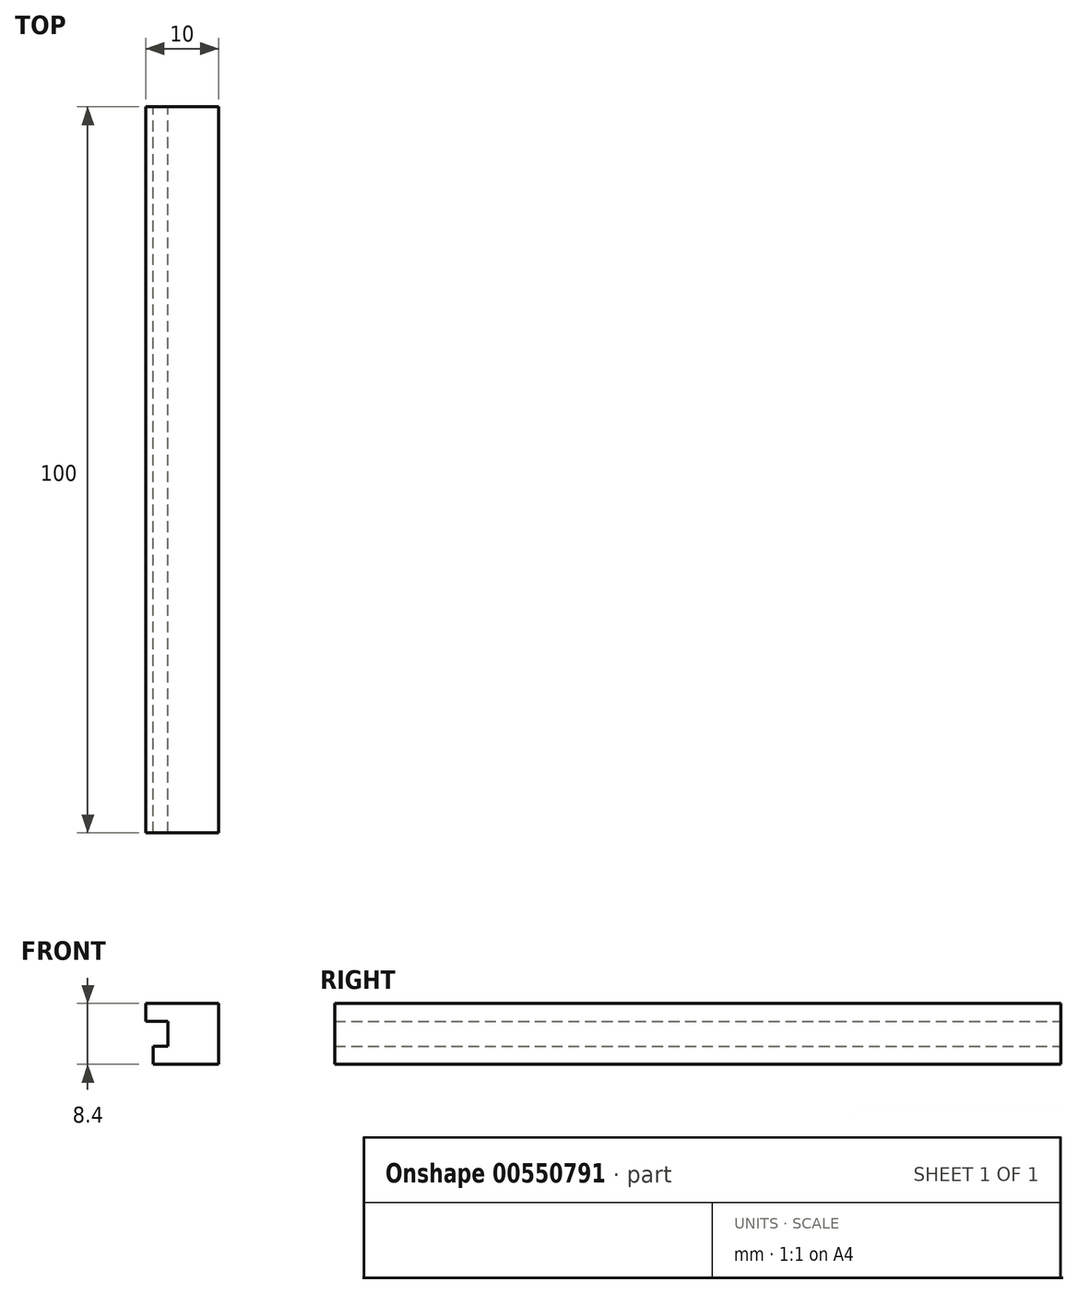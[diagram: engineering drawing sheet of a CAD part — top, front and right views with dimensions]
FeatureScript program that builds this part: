
annotation { "Feature Type Name" : "Feature", "Feature Type Description" : "" }
export const myFeature = defineFeature(function(context is Context, id is Id, definition is map)
    precondition{}
    {
        {
            var Q0;
            Q0=qCreatedBy(makeId("Front.planeOp"),FACE);
            var sketch = newSketch(context, id + "F0", { "sketchPlane" : qUnion([Q0])});
            skLineSegment(sketch, "E0", {"start": v(-46.22, 39.94) * mm, "end": v(-36.22, 39.94) * mm});
            skLineSegment(sketch, "E1", {"start": v(-36.22, 39.94) * mm, "end": v(-36.22, 31.54) * mm});
            skLineSegment(sketch, "E2", {"start": v(-36.22, 31.54) * mm, "end": v(-45.22, 31.54) * mm});
            skLineSegment(sketch, "E3", {"start": v(-45.22, 31.54) * mm, "end": v(-45.22, 34.04) * mm});
            skLineSegment(sketch, "E4", {"start": v(-45.22, 34.04) * mm, "end": v(-43.22, 34.04) * mm});
            skLineSegment(sketch, "E5", {"start": v(-43.22, 34.04) * mm, "end": v(-43.22, 37.44) * mm});
            skLineSegment(sketch, "E6", {"start": v(-43.22, 37.44) * mm, "end": v(-46.22, 37.44) * mm});
            skLineSegment(sketch, "E7", {"start": v(-46.22, 37.44) * mm, "end": v(-46.22, 39.94) * mm});
            skSolve(sketch);
        }
        {
            var Q0;
            Q0=makeQuery(id+"F0.imprint","IMPRINT",FACE,{"disambiguationData":[TD([[makeQuery(id+"F0.imprint","IMPRINT",EDGE,{"derivedFrom":sQuery(id+"F0.wireOp",EDGE,"E0")}),-1.0]])]});
            extrude(context, id + "F1", {"entities" : qUnion([Q0]), "depth" : 100 * mm, "offsetDistance" : 25 * mm});
        }
    });
